# Revit family: 94700-111
name_source: partatom
category: Equipamento especial
revit_build: Autodesk Revit 2016 (Build: 20150220_1215(x64)
units: mm (PartAtom-declared; Revit-internal decimal feet)

## family parameters
Com base no plano de trabalho = Não
Compartilhado = Não
Corte com vazios quando carregados = Não
Cota do conector redondo = Utilizar diâmetro
Ponto de cálculo do ambiente = Não
Sempre na vertical = Sim
Tipo de parte = Normal

## types (1)
- Tramontina - 94700-111
    Classe de Construção = Classe 2
    Consumo máximo = 3,80 kWh
    Código de montagem = 94700/111
    Descrição = Tramontina Cooktop a Gás
    Desenvolvedor = Factory Cursos & Desenvolvimento
    Eficiência Energética = D
    Fabricante = Tramontina
    Frequência = 50 - 60 Hz
    Modelo = Tramontina - Dominó 1GX tri 30
    Peso Bruto = 4,9 kg
    Peso liquido = 4 kg
    Potência Máx. Tripla Chama = 3,80 kW
    Potência elétrica = 5 kW
    Rendimento Médio = 58%
    Site do desenvolvedor = www.factorycursos.com.br
    Tensão = 127 -  220 V
    Tipo de imagem = <Nenhum>
    URL = www.tramontina.com.br
